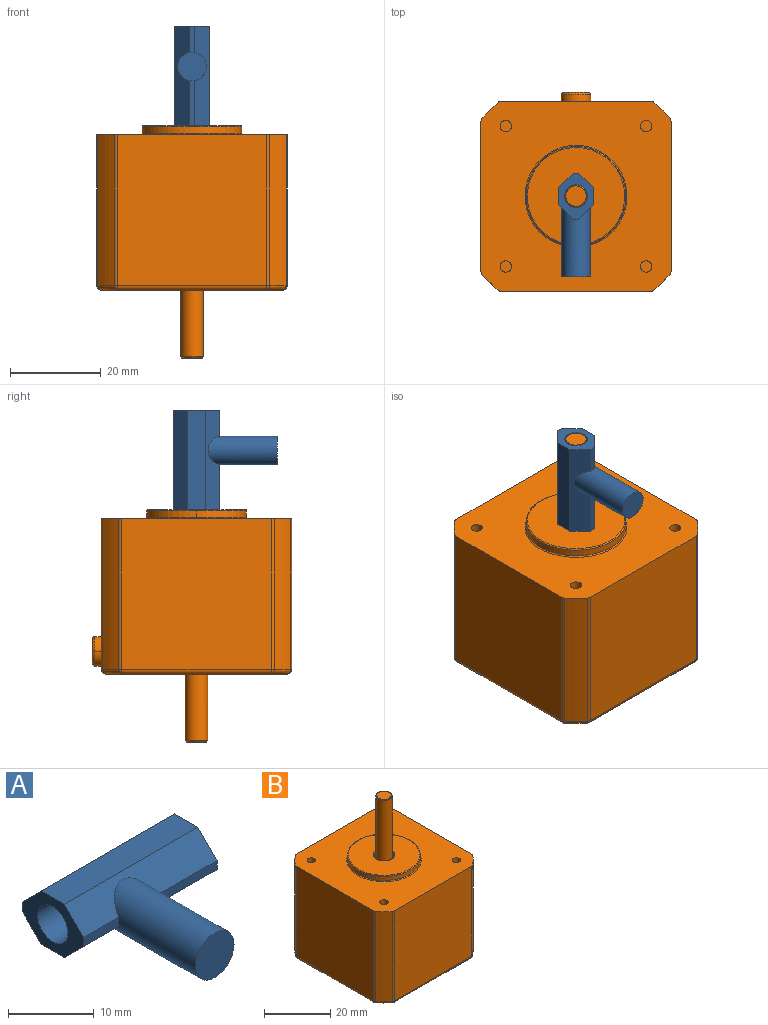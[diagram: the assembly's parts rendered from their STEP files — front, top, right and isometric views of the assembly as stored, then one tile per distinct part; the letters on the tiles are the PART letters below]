
ASSEMBLY  parts=2 mates=1
PART A: 14 faces, bbox 22x22.9x7.6 mm
  f0: plane 9.97x1.27mm, normal (0,-1,0), area 12.6mm2, adj f1,f8,f10,f11
  f1: plane 10.16x7.62mm, normal (1,0,0), area 37.6mm2, adj f0,f2,f5,f6,f7,f10,f11,f12
  f2: plane 22x3.81mm, normal (0,0,1), area 83.8mm2, adj f1,f3,f10,f13
  f3: plane 10.16x7.62mm, normal (-1,0,0), area 37.6mm2, adj f2,f4,f5,f6,f7,f10,f11,f12
  f4: plane 5.81x1.27mm, normal (0,-1,0), area 7.3mm2, adj f3,f8,f10,f11
  f5: plane 22x1.27mm, normal (0,1,0), area 27.9mm2, adj f1,f3,f12,f13
  f6: plane 22x3.81mm, normal (0,0,-1), area 83.8mm2, adj f1,f3,f11,f12
  f7: cylinder r=2.5mm len=22mm, axis (-1,0,0), area 345.6mm2, adj f1,f3
  f8: cylinder r=3.17mm len=15.25mm, axis (0,1,0), area 281.8mm2, adj f0,f4,f9,f10,f11
  f9: plane 6.35x6.35mm, normal (0,-1,0), area 31.7mm2, adj f8
  f10: plane 22x3.18mm, normal (0,-0.71,0.71), area 82.1mm2, adj f0,f1,f2,f3,f4,f8
  f11: plane 22x3.18mm, normal (0,-0.71,-0.71), area 82.1mm2, adj f0,f1,f3,f4,f6,f8
  f12: plane 22x3.18mm, normal (0,0.71,-0.71), area 98.8mm2, adj f1,f3,f5,f6
  f13: plane 22x3.18mm, normal (0,0.71,0.71), area 98.8mm2, adj f1,f2,f3,f5
PART B: 105 faces, bbox 46x48x77.3 mm
  f0: plane 4.5x4.5mm, normal (0,0,-1), area 15.9mm2, adj f1,f104
  f1: revolved ~5x2.5mm, area 2.6mm2, adj f0,f2,f104
  f2: revolved ~16.75x5mm, area 526.2mm2, adj f1,f3,f104
  f3: plane 6x6mm, normal (0,0,-1), area 8.6mm2, adj f2,f4,f103
  f4: revolved ~6x3mm, area 7.1mm2, adj f3,f5,f103
  f5: revolved ~6.5x6.5mm, area 7.6mm2, adj f4,f6,f103
  f6: plane 15.5x15.5mm, normal (0,0,-1), area 155.5mm2, adj f5,f7
  f7: revolved ~16x16mm, area 19.5mm2, adj f6,f8,f102
  f8: revolved ~16x8mm, area 18.8mm2, adj f7,f9,f102
  f9: plane 44x44mm, normal (0,0,-1), area 1218.6mm2, adj f8,f10,f63,f64,f65,f66,f67,f68
  f10: revolved ~4.27x4.27mm, area 8mm2, adj f9,f11,f61,f62
  f11: revolved ~33.3x3.63mm, area 171.3mm2, adj f10,f12,f39,f60
  f12: revolved ~33.3x0.64mm, area 23mm2, adj f11,f13,f39,f62
  f13: plane 37.3x37.01mm, normal (0,1,0), area 1065.9mm2, adj f12,f14,f32,f38,f39,f63
  f14: revolved ~33.3x2mm, area 29.3mm2, adj f13,f15,f16,f39
  f15: revolved ~1x1mm, area 0.7mm2, adj f14,f63,f64
  f16: revolved ~33.3x3.63mm, area 171.3mm2, adj f14,f17,f39,f64
  f17: revolved ~33.3x0.64mm, area 23mm2, adj f16,f18,f31,f39
  f18: plane 37.3x37.01mm, normal (-1,0,0), area 1099.1mm2, adj f17,f19,f39,f65
  f19: revolved ~33.3x2mm, area 29.3mm2, adj f18,f20,f30,f39
  f20: revolved ~33.3x3.63mm, area 171.3mm2, adj f19,f21,f39,f66
  f21: revolved ~33.3x0.64mm, area 23mm2, adj f20,f22,f29,f39
  f22: plane 37.3x37.01mm, normal (0,-1,0), area 1099.1mm2, adj f21,f23,f39,f67
  f23: revolved ~33.3x2mm, area 29.3mm2, adj f22,f24,f25,f39
  f24: revolved ~1x1mm, area 0.7mm2, adj f23,f67,f68
  f25: revolved ~33.3x3.63mm, area 171.3mm2, adj f23,f26,f39,f68
  f26: revolved ~33.3x0.64mm, area 23mm2, adj f25,f27,f28,f39
  f27: plane 37.3x37.01mm, normal (1,0,0), area 1099.1mm2, adj f26,f39,f60,f69
  f28: revolved ~1x1mm, area 0.7mm2, adj f26,f68,f69
  f29: revolved ~1x1mm, area 0.7mm2, adj f21,f66,f67
  f30: revolved ~1x1mm, area 0.7mm2, adj f19,f65,f66
  f31: revolved ~1x1mm, area 0.7mm2, adj f17,f64,f65
  f32: revolved ~6.5x3.25mm, area 15.3mm2, adj f13,f33,f38
  f33: revolved ~6.5x6.5mm, area 15.1mm2, adj f32,f34,f38
  f34: revolved ~5.5x5.5mm, area 11.9mm2, adj f33,f35,f37
  f35: revolved ~4.52x2.26mm, area 10.7mm2, adj f34,f36,f37
  f36: plane 4.52x4.52mm, normal (0,1,0), area 16mm2, adj f35,f37
  f37: revolved ~4.52x2.26mm, area 10.7mm2, adj f34,f35,f36
  f38: revolved ~6.5x3.25mm, area 15.3mm2, adj f13,f32,f33
  f39: plane 42x42mm, normal (0,0,1), area 1314.9mm2, adj f11,f12,f13,f14,f16,f17,f18,f19
  f40: revolved ~5x2.5mm, area 39.3mm2, adj f39,f41
  f41: plane 2.5x2.5mm, normal (0,0,1), area 4.9mm2, adj f40
  f42: revolved ~5x2.5mm, area 39.3mm2, adj f39,f43
  f43: plane 2.5x2.5mm, normal (0,0,1), area 4.9mm2, adj f42
  f44: revolved ~5x2.5mm, area 39.3mm2, adj f39,f45
  f45: plane 2.5x2.5mm, normal (0,0,1), area 4.9mm2, adj f44
  f46: revolved ~5x2.5mm, area 39.3mm2, adj f39,f47
  f47: plane 2.5x2.5mm, normal (0,0,1), area 4.9mm2, adj f46
  f48: revolved ~22.5x22.5mm, area 27.4mm2, adj f39,f49,f59
  f49: revolved ~22x11mm, area 51.8mm2, adj f48,f50,f59
  f50: revolved ~22x22mm, area 26.9mm2, adj f49,f51,f59
  f51: plane 21.5x21.5mm, normal (0,0,1), area 329.9mm2, adj f50,f52
  f52: revolved ~6.5x6.5mm, area 7.6mm2, adj f51,f53
  f53: revolved ~6x6mm, area 33mm2, adj f52,f54
  f54: plane 6x6mm, normal (0,0,1), area 8.6mm2, adj f53,f55
  f55: revolved ~23.75x5mm, area 746.1mm2, adj f54,f56,f58
  f56: revolved ~5x2.5mm, area 2.6mm2, adj f55,f57,f58
  f57: plane 4.5x4.5mm, normal (0,0,1), area 15.9mm2, adj f56,f58
  f58: revolved ~5x2.5mm, area 2.6mm2, adj f55,f56,f57
  f59: revolved ~22x11mm, area 51.8mm2, adj f48,f49,f50
  f60: revolved ~33.3x2mm, area 29.3mm2, adj f11,f27,f39,f61
  f61: revolved ~1x1mm, area 0.7mm2, adj f10,f60,f69
  f62: revolved ~1x1mm, area 0.7mm2, adj f10,f12,f63
  f63: revolved ~33.01x2mm, area 155.5mm2, adj f9,f13,f15,f62
  f64: revolved ~4.27x4.27mm, area 8mm2, adj f9,f15,f16,f31
  f65: revolved ~33.01x2mm, area 155.5mm2, adj f9,f18,f30,f31
  f66: revolved ~4.27x4.27mm, area 8mm2, adj f9,f20,f29,f30
  f67: revolved ~33.01x2mm, area 155.5mm2, adj f9,f22,f24,f29
  f68: revolved ~4.27x4.27mm, area 8mm2, adj f9,f24,f25,f28
  f69: revolved ~33.01x2mm, area 155.5mm2, adj f9,f27,f28,f61
  f70: revolved ~7.08x7.08mm, area 15.9mm2, adj f9,f71,f77
  f71: revolved ~6.08x3.04mm, area 28.7mm2, adj f70,f72,f77
  f72: plane 6.08x6.08mm, normal (0,0,-1), area 12.5mm2, adj f71,f73,f76,f77
  f73: revolved ~4.59x3mm, area 21.7mm2, adj f72,f74,f76
  f74: revolved ~4.59x4.59mm, area 10.4mm2, adj f73,f75,f76
  f75: plane 3.6x3.59mm, normal (0,0,-1), area 10.1mm2, adj f74
  f76: revolved ~4.59x3mm, area 21.7mm2, adj f72,f73,f74
  f77: revolved ~6.08x3.04mm, area 28.7mm2, adj f70,f71,f72
  f78: revolved ~7.08x7.08mm, area 15.9mm2, adj f9,f79,f85
  f79: revolved ~6.08x3.04mm, area 28.7mm2, adj f78,f80,f85
  f80: plane 6.08x6.08mm, normal (0,0,-1), area 12.5mm2, adj f79,f81,f84,f85
  f81: revolved ~4.59x3mm, area 21.7mm2, adj f80,f82,f84
  f82: revolved ~4.59x4.59mm, area 10.4mm2, adj f81,f83,f84
  f83: plane 3.6x3.59mm, normal (0,0,-1), area 10.1mm2, adj f82
  f84: revolved ~4.59x3mm, area 21.7mm2, adj f80,f81,f82
  f85: revolved ~6.08x3.04mm, area 28.7mm2, adj f78,f79,f80
  f86: revolved ~7.08x7.08mm, area 15.9mm2, adj f9,f87,f93
  f87: revolved ~6.08x3.04mm, area 28.7mm2, adj f86,f88,f93
  f88: plane 6.08x6.08mm, normal (0,0,-1), area 12.5mm2, adj f87,f89,f92,f93
  f89: revolved ~4.59x3mm, area 21.7mm2, adj f88,f90,f92
  f90: revolved ~4.59x4.59mm, area 10.4mm2, adj f89,f91,f92
  f91: plane 3.6x3.59mm, normal (0,0,-1), area 10.1mm2, adj f90
  f92: revolved ~4.59x3mm, area 21.7mm2, adj f88,f89,f90
  f93: revolved ~6.08x3.04mm, area 28.7mm2, adj f86,f87,f88
  f94: revolved ~7.08x7.08mm, area 15.9mm2, adj f9,f95,f101
  f95: revolved ~6.08x3.04mm, area 28.7mm2, adj f94,f96,f101
  f96: plane 6.08x6.08mm, normal (0,0,-1), area 12.5mm2, adj f95,f97,f100,f101
  f97: revolved ~4.59x3mm, area 21.7mm2, adj f96,f98,f100
  f98: revolved ~4.59x4.59mm, area 10.4mm2, adj f97,f99,f100
  f99: plane 3.6x3.59mm, normal (0,0,-1), area 10.1mm2, adj f98
  f100: revolved ~4.59x3mm, area 21.7mm2, adj f96,f97,f98
  f101: revolved ~6.08x3.04mm, area 28.7mm2, adj f94,f95,f96
  f102: revolved ~16x8mm, area 18.8mm2, adj f7,f8,f9
  f103: revolved ~6x3mm, area 7.1mm2, adj f3,f4,f5
  f104: revolved ~5x2.5mm, area 2.6mm2, adj f0,f1,f2
PLACE A rot(axis=(0,1,0),90deg) t=(13.3,0,-53.3)mm
PLACE B at identity fixed
MATE revolute A.f7 <-> B.f57  axis (0,0,1) through (0,0,24)mm
